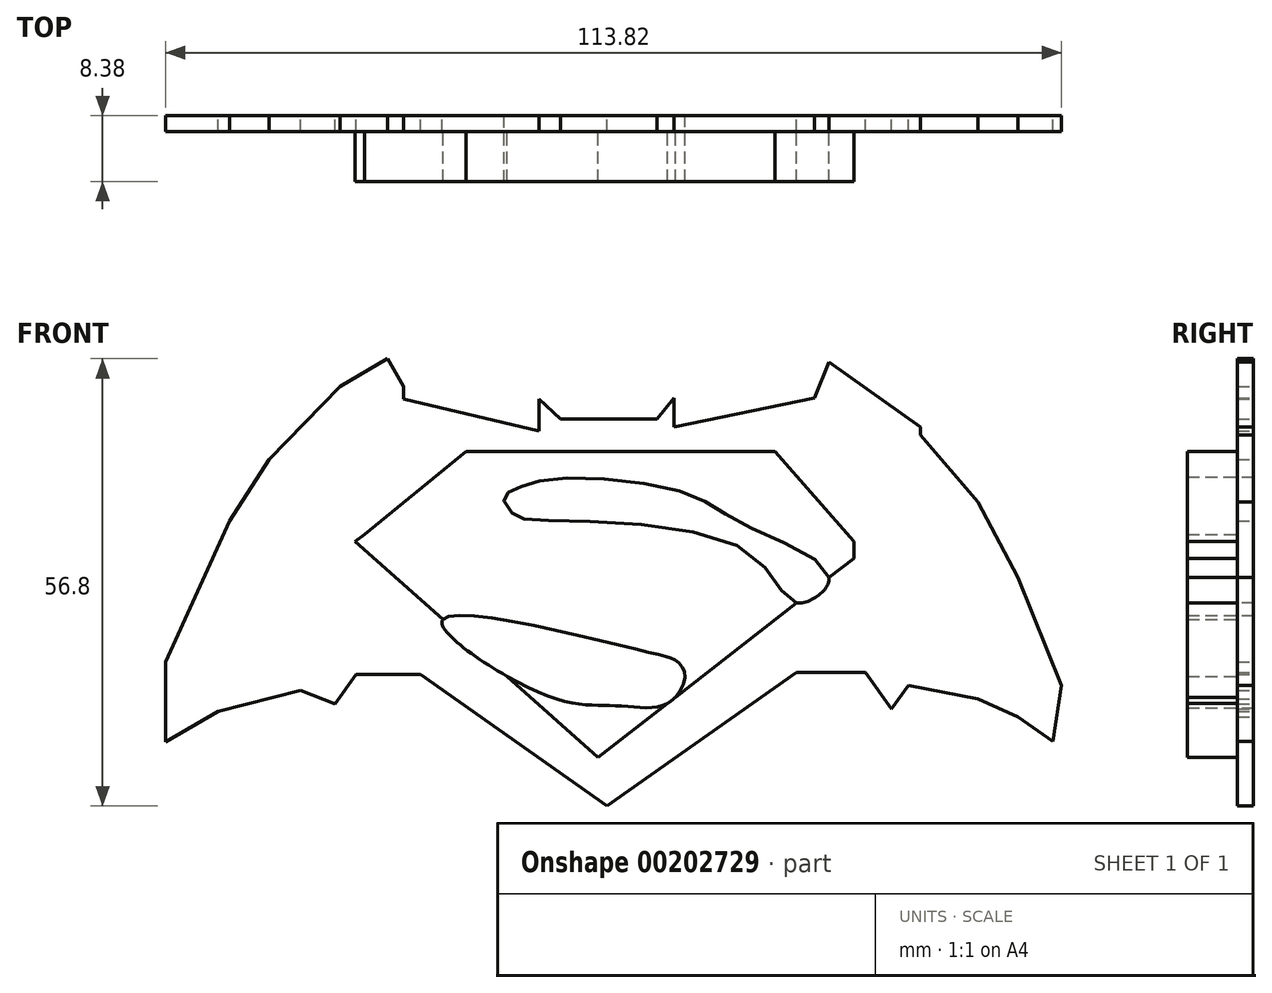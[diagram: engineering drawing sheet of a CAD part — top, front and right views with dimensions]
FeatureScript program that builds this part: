
annotation { "Feature Type Name" : "Feature", "Feature Type Description" : "" }
export const myFeature = defineFeature(function(context is Context, id is Id, definition is map)
    precondition{}
    {
        {
            var Q0;
            Q0=qCreatedBy(makeId("Front.planeOp"),FACE);
            var sketch = newSketch(context, id + "F0", { "sketchPlane" : qUnion([Q0])});
            skLineSegment(sketch, "E0", {"start": v(-24.96, -12.31) * mm, "end": v(-1.27, -29) * mm});
            skLineSegment(sketch, "E1", {"start": v(-1.27, -29) * mm, "end": v(22.82, -12.05) * mm});
            skLineSegment(sketch, "E2", {"start": v(22.82, -12.05) * mm, "end": v(31.57, -12.05) * mm});
            skLineSegment(sketch, "E3", {"start": v(-24.96, -12.31) * mm, "end": v(-33.17, -12.31) * mm});
            skLineSegment(sketch, "E4", {"start": v(-33.17, -12.31) * mm, "end": v(-35.8, -16.06) * mm});
            skLineSegment(sketch, "E5", {"start": v(-35.8, -16.06) * mm, "end": v(-40.16, -14.33) * mm});
            skLineSegment(sketch, "E6", {"start": v(-40.16, -14.33) * mm, "end": v(-50.66, -17.02) * mm});
            skLineSegment(sketch, "E7", {"start": v(-50.66, -17.02) * mm, "end": v(-55.78, -19.99) * mm});
            skLineSegment(sketch, "E8", {"start": v(31.57, -12.05) * mm, "end": v(34.86, -16.72) * mm});
            skLineSegment(sketch, "E9", {"start": v(34.86, -16.72) * mm, "end": v(37, -13.68) * mm});
            skLineSegment(sketch, "E10", {"start": v(37, -13.68) * mm, "end": v(45.83, -15.4) * mm});
            skLineSegment(sketch, "E11", {"start": v(45.83, -15.4) * mm, "end": v(50.95, -17.7) * mm});
            skLineSegment(sketch, "E12", {"start": v(50.95, -17.7) * mm, "end": v(55.38, -20.82) * mm});
            skLineSegment(sketch, "E13", {"start": v(55.38, -20.82) * mm, "end": v(56.47, -13.68) * mm});
            skLineSegment(sketch, "E14", {"start": v(56.47, -13.68) * mm, "end": v(50.95, 0) * mm});
            skLineSegment(sketch, "E15", {"start": v(50.95, 0) * mm, "end": v(45.83, 9.62) * mm});
            skLineSegment(sketch, "E16", {"start": v(45.83, 9.62) * mm, "end": v(38.57, 18.1) * mm});
            skLineSegment(sketch, "E17", {"start": v(38.57, 19.14) * mm, "end": v(26.91, 27.35) * mm});
            skLineSegment(sketch, "E18", {"start": v(26.91, 27.35) * mm, "end": v(38.57, 19.14) * mm});
            skLineSegment(sketch, "E19", {"start": v(38.57, 19.14) * mm, "end": v(38.57, 18.1) * mm});
            skLineSegment(sketch, "E20", {"start": v(26.91, 27.35) * mm, "end": v(25.05, 22.81) * mm});
            skLineSegment(sketch, "E21", {"start": v(25.05, 22.81) * mm, "end": v(7.25, 19.14) * mm});
            skLineSegment(sketch, "E22", {"start": v(7.25, 19.14) * mm, "end": v(7.25, 22.81) * mm});
            skLineSegment(sketch, "E23", {"start": v(-55.78, -19.99) * mm, "end": v(-57.35, -20.9) * mm});
            skLineSegment(sketch, "E24", {"start": v(-57.35, -20.9) * mm, "end": v(-57.35, -10.7) * mm});
            skLineSegment(sketch, "E25", {"start": v(-57.35, -10.7) * mm, "end": v(-49.18, 7.2) * mm});
            skLineSegment(sketch, "E26", {"start": v(-49.18, 7.2) * mm, "end": v(-44.2, 15) * mm});
            skLineSegment(sketch, "E27", {"start": v(-44.2, 15) * mm, "end": v(-35.18, 24.3) * mm});
            skLineSegment(sketch, "E28", {"start": v(-35.18, 24.3) * mm, "end": v(-29.13, 27.8) * mm});
            skLineSegment(sketch, "E29", {"start": v(-29.13, 27.8) * mm, "end": v(-27.1, 24.3) * mm});
            skLineSegment(sketch, "E30", {"start": v(-27.1, 24.3) * mm, "end": v(-27.1, 22.68) * mm});
            skLineSegment(sketch, "E31", {"start": v(-27.1, 22.68) * mm, "end": v(-9.88, 18.64) * mm});
            skLineSegment(sketch, "E32", {"start": v(-9.88, 18.64) * mm, "end": v(-9.88, 22.68) * mm});
            skLineSegment(sketch, "E33", {"start": v(-9.88, 22.68) * mm, "end": v(-7.2, 20.12) * mm});
            skLineSegment(sketch, "E34", {"start": v(-7.2, 20.12) * mm, "end": v(5.06, 20.12) * mm});
            skLineSegment(sketch, "E35", {"start": v(5.06, 20.12) * mm, "end": v(7.25, 22.81) * mm});
            skLineSegment(sketch, "E36", {"start": v(20.06, 16.05) * mm, "end": v(-19.17, 16.05) * mm});
            skLineSegment(sketch, "E37", {"start": v(-19.17, 16.05) * mm, "end": v(-32.1, 5.45) * mm});
            skLineSegment(sketch, "E38", {"start": v(-32.1, 5.45) * mm, "end": v(-33.29, 4.61) * mm});
            skLineSegment(sketch, "E39", {"start": v(-33.29, 4.61) * mm, "end": v(-2.4, -22.83) * mm});
            skLineSegment(sketch, "E40", {"start": v(-2.4, -22.83) * mm, "end": v(30.1, 2.46) * mm});
            skLineSegment(sketch, "E41", {"start": v(20.06, 16.05) * mm, "end": v(30.1, 4.61) * mm});
            skLineSegment(sketch, "E42", {"start": v(30.1, 2.46) * mm, "end": v(30.1, 4.61) * mm});
            skFitSpline(sketch, "E43", {"points": [v(26.94, 0) * mm, v(16.43, 6.6) * mm, v(8.62, 10.76) * mm, v(-8.3, 12.55) * mm, v(-13, 11.22) * mm, v(-14.42, 10.2) * mm, v(-13.3, 8.17) * mm, v(-9.94, 7.32) * mm, v(16.67, 3.26) * mm, v(22.83, -3.2) * mm, v(26.94, 0) * mm]});
            skFitSpline(sketch, "E44", {"points": [v(-22.12, -5.3) * mm, v(3.21, -9.3) * mm, v(7.5, -10.58) * mm, v(8.64, -12.32) * mm, v(6.4, -15.98) * mm, v(0, -16.29) * mm, v(-9.2, -14.88) * mm, v(-22.12, -5.3) * mm]});
            skSolve(sketch);
        }
        {
            var Q0;
            Q0 = qSketchRegion(id + "F0", true);
            extrude(context, id + "F1", {"entities" : qUnion([Q0]), "depth" : 2.03 * mm});
        }
        {
            var Q0;
            Q0=makeQuery(id+"F0.imprint","IMPRINT",FACE,{"disambiguationData":[TD([[makeQuery(id+"F0.imprint","IMPRINT",EDGE,{"derivedFrom":sQuery(id+"F0.wireOp",EDGE,"E36")}),1.0]])]});
            var Q1;
            {var subQ0=sQuery(id+"F0.wireOp",EDGE,"E40");var subQ1=sQuery(id+"F0.wireOp",EDGE,"E39");var subQ2=makeQuery(id+"F0.imprint","INTERSECT",VERTEX,{"derivedFrom":[subQ1,subQ0]});Q1=makeQuery(id+"F0.imprint","IMPRINT",FACE,{"disambiguationData":[TD([[makeQuery(id+"F0.imprint","IMPRINT",EDGE,{"disambiguationData":[TD([[subQ2,1.0]])],"derivedFrom":subQ1}),1.0]])]});}
            extrude(context, id + "F2", {"entities" : qUnion([Q0, Q1]), "operationType" : NewBodyOperationType.ADD, "depth" : 8.38 * mm});
        }
    });
